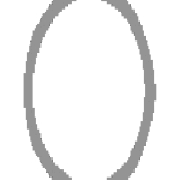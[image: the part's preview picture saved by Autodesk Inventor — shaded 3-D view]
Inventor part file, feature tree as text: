
AUTODESK INVENTOR PART (.ipt)
format: ipt  version: 2021 (Build 250183000, 183)  size: 109,056 bytes
history: native  units: in
note: dims shown in document units (in); Inventor stores cm internally (conversion verified against a paired STEP export)
features: other x4, sketch x3, plane x1
ambient origin geometry x8: Origin, YZ Plane, XZ Plane, XY Plane, X Axis, Y Axis, Z Axis, Center Point
bodies: Solid1 (feature_tree), Body (feature_tree)
feature tree (8):
  other  "Driven Length"
  other  "Frame Generator"
  other  "Start Plane"
  other  "End Plane"
  sketch  "Sketch"  dims[d2=29.4in d4=-0.0in d5=29.4in d6=0.12in d7=0.0in d8=90.0deg d9=29.4in]
  sketch  "Sketch2"  dims[d0=1.0in]
  plane  "Work Plane3"
  sketch  "Sketch3"  dims[d1=0.065in]
